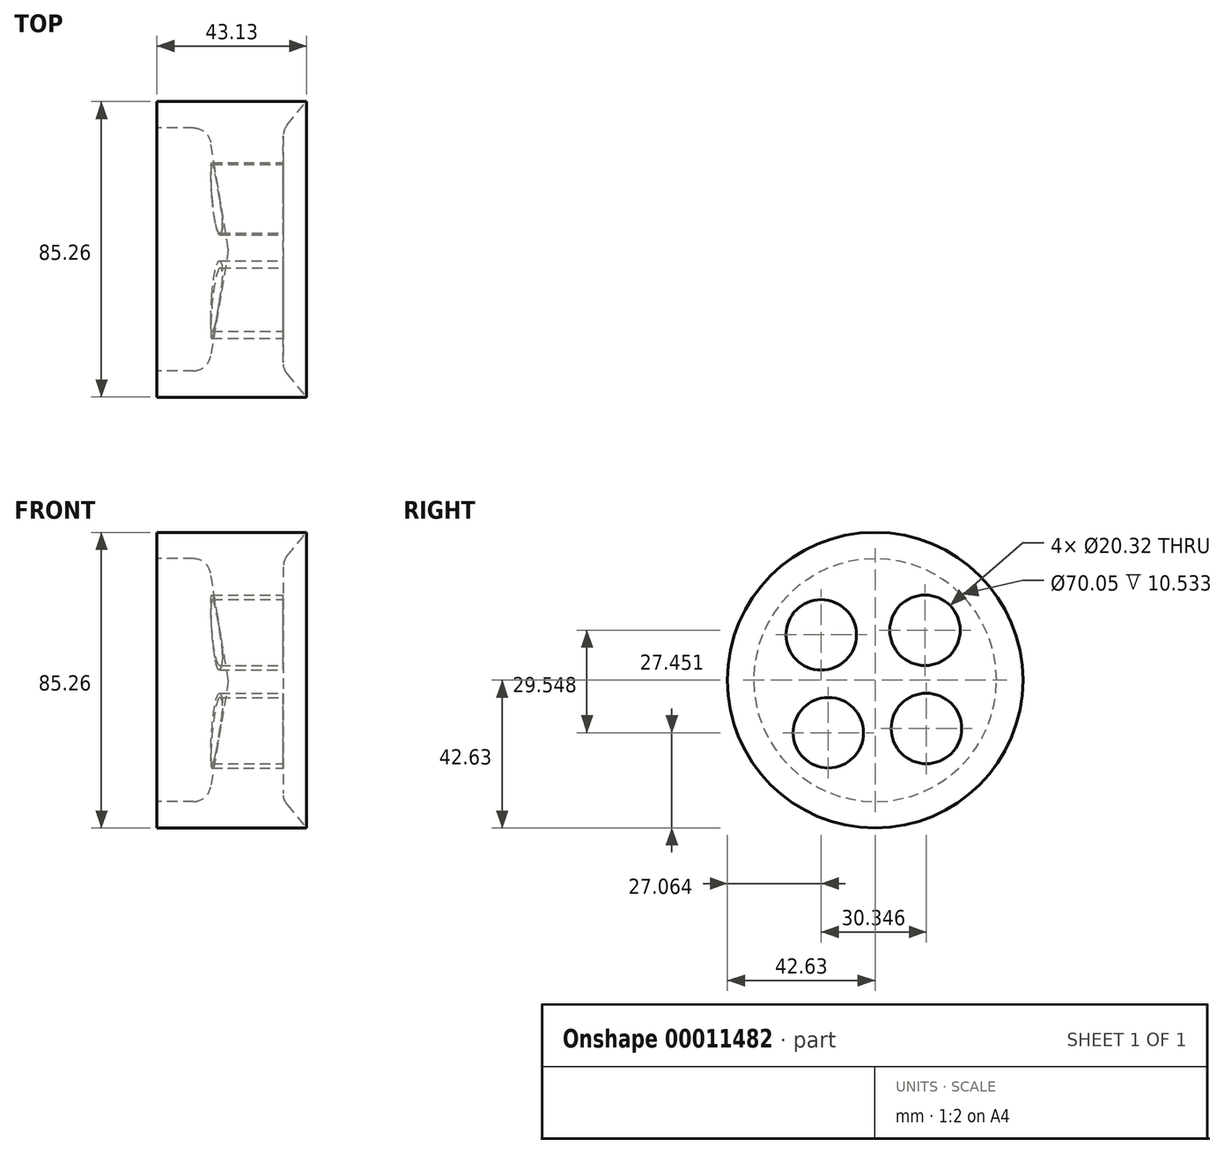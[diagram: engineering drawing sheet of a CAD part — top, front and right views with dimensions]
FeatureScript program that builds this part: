
annotation { "Feature Type Name" : "Feature", "Feature Type Description" : "" }
export const myFeature = defineFeature(function(context is Context, id is Id, definition is map)
    precondition{}
    {
        {
            var Q0;
            Q0=qCreatedBy(makeId("Front.planeOp"),FACE);
            var sketch = newSketch(context, id + "F0", { "sketchPlane" : qUnion([Q0])});
            skLineSegment(sketch, "E0", {"start": v(-69.9, 0) * mm, "end": v(116.97, 0) * mm, "construction": true});
            skLineSegment(sketch, "E1", {"start": v(49.15, 0) * mm, "end": v(49.15, 34.51) * mm});
            skLineSegment(sketch, "E2", {"start": v(49.15, 34.51) * mm, "end": v(55.83, 42.63) * mm});
            skLineSegment(sketch, "E3", {"start": v(55.83, 42.63) * mm, "end": v(12.7, 42.63) * mm});
            skLineSegment(sketch, "E4", {"start": v(12.7, 42.63) * mm, "end": v(12.7, 35.03) * mm});
            skLineSegment(sketch, "E5", {"start": v(12.7, 35.03) * mm, "end": v(23.24, 35.03) * mm});
            skLineSegment(sketch, "E6", {"start": v(28.17, 30.85) * mm, "end": v(33.3, 0) * mm});
            skLineSegment(sketch, "E7", {"start": v(33.3, 0) * mm, "end": v(49.15, 0) * mm});
            skPoint(sketch, "E8.visualSharp", {"position": v(27.47, 35.03) * mm});
            skArc(sketch, "E8.filletArc", {"start": v(28.17, 30.85) * mm, "mid": v(26.47, 33.84) * mm, "end": v(23.24, 35.03) * mm});
            skSolve(sketch);
        }
        {
            var Q0;
            Q0=makeQuery(id+"F0.imprint","IMPRINT",FACE,{"disambiguationData":[TD([[makeQuery(id+"F0.imprint","IMPRINT",EDGE,{"derivedFrom":sQuery(id+"F0.wireOp",EDGE,"E1")}),1.0]])]});
            var Q1;
            Q1=sQuery(id+"F0.wireOp",EDGE,"E0");
            revolve(context, id + "F1", {"entities" : qUnion([Q0]), "axis" : qUnion([Q1]), "revolveType" : RevolveType.FULL});
        }
        {
            var Q0;
            Q0=makeQuery(id+"F1.opRevolve","SWEPT_FACE",FACE,{"disambiguationData":[OSD([sQuery(id+"F0.wireOp",EDGE,"E1")])]});
            var sketch = newSketch(context, id + "F2", { "sketchPlane" : qUnion([Q0])});
            skCircle(sketch, "E9", {"center": v(14.37, 14.37) * mm, "radius": 10.16 * mm});
            skLineSegment(sketch, "E10", {"start": v(14.37, 14.37) * mm, "end": v(0, 0) * mm, "construction": true});
            skLineSegment(sketch, "E11", {"start": v(0, 0) * mm, "end": v(50.2, 0) * mm, "construction": true});
            skCircle(sketch, "E12.1.0", {"center": v(14.78, -13.94) * mm, "radius": 10.16 * mm});
            skCircle(sketch, "E12.2.0", {"center": v(-13.5, -15.18) * mm, "radius": 10.16 * mm});
            skCircle(sketch, "E12.3.0", {"center": v(-15.57, 13.06) * mm, "radius": 10.16 * mm});
            skPoint(sketch, "E12.center", {"position": v(0, 0) * mm});
            skLineSegment(sketch, "E12.anchor1", {"start": v(0, 0) * mm, "end": v(14.37, 14.37) * mm, "construction": true});
            skLineSegment(sketch, "E12.anchor2", {"start": v(0, 0) * mm, "end": v(-15.57, 13.06) * mm, "construction": true});
            skSolve(sketch);
        }
        {
            var Q0;
            Q0=makeQuery(id+"F2.imprint","IMPRINT",FACE,{"disambiguationData":[TD([[makeQuery(id+"F2.imprint","IMPRINT",EDGE,{"derivedFrom":sQuery(id+"F2.wireOp",EDGE,"E9")}),1.0]])]});
            var Q1;
            Q1=makeQuery(id+"F2.imprint","IMPRINT",FACE,{"disambiguationData":[TD([[makeQuery(id+"F2.imprint","IMPRINT",EDGE,{"derivedFrom":sQuery(id+"F2.wireOp",EDGE,"E12.1.0")}),1.0]])]});
            var Q2;
            Q2=makeQuery(id+"F2.imprint","IMPRINT",FACE,{"disambiguationData":[TD([[makeQuery(id+"F2.imprint","IMPRINT",EDGE,{"derivedFrom":sQuery(id+"F2.wireOp",EDGE,"E12.3.0")}),1.0]])]});
            var Q3;
            Q3=makeQuery(id+"F2.imprint","IMPRINT",FACE,{"disambiguationData":[TD([[makeQuery(id+"F2.imprint","IMPRINT",EDGE,{"derivedFrom":sQuery(id+"F2.wireOp",EDGE,"E12.2.0")}),1.0]])]});
            extrude(context, id + "F3", {"entities" : qUnion([Q0, Q1, Q2, Q3]), "operationType" : NewBodyOperationType.REMOVE, "endBound" : BoundingType.THROUGH_ALL, "oppositeDirection" : true, "depth" : 25.4 * mm});
        }
        {
            var Q0;
            Q0=makeQuery(id+"F1.opRevolve","SWEPT_EDGE",EDGE,{"disambiguationData":[OSD([sQuery(id+"F0.wireOp",EDGE,"E1"),sQuery(id+"F0.wireOp",EDGE,"E2")])]});
            fillet(context, id + "F4", {"entities" : qUnion([Q0]), "radius" : 5.08 * mm, "tangentPropagation" : true, "rho" : 0.5, "crossSection" : FilletCrossSection.CONIC, "allowEdgeOverflow" : false});
        }
    });
